# Revit family: 931120001_Desagüe Sencillo
name_source: partatom
category: Plumbing Fixtures
units: mm (PartAtom-declared; Revit-internal decimal feet)

## family parameters
Always vertical = Yes
Cut with Voids When Loaded = No
OmniClass Number = 23.27.43.00
OmniClass Title = Pipe Fittings
Part Type = Normal
Room Calculation Point = No
Round Connector Dimension = Use Diameter
Shared = No
Work Plane-Based = No

## types (1)
- 931120001_Desagüe Sencillo
    Alto = 206 mm
    Creado por = BIMBAU
    Default Elevation = 0 mm  [stored 0 ft]
    Description = Para la fabricación de este producto se utilizan materiales,
equipos y tecnologías de última generación, que permiten
ofrecer un artículo con los más altos estándares de calidad.
    Diametro_2 = 31 mm  [stored 0.101706 ft]
    Diámetro = 25 mm  [stored 0.082021 ft]
    Diámetro_1 = 53 mm
    Fecha de creación = 7/04/2021
    Garantía = 30 Años
    Material = Corona_Cromado
    Normatividad = IAPMO IGC 157
    Referencia = 931120001
    Resistencia = Resistente a la corrosión, pelado y decoloración por agua. Resistente al efecto de jabones y limpiadores de tocador.
    URL = https://www.grival.com
    Uso = Residencial
    Ventajas = Permite drenar el agua rápidamente. Elaborado en resina de alta ingeniería.
Fácil instalación, limpieza y mantenimiento.

note: [stored X ft] marks values corroborated as IEEE doubles in the binary element streams (Revit-internal decimal feet)

## geometry (parser evidence)
native form markers: Sweep x2
no freeform markers — native parametric forms only
